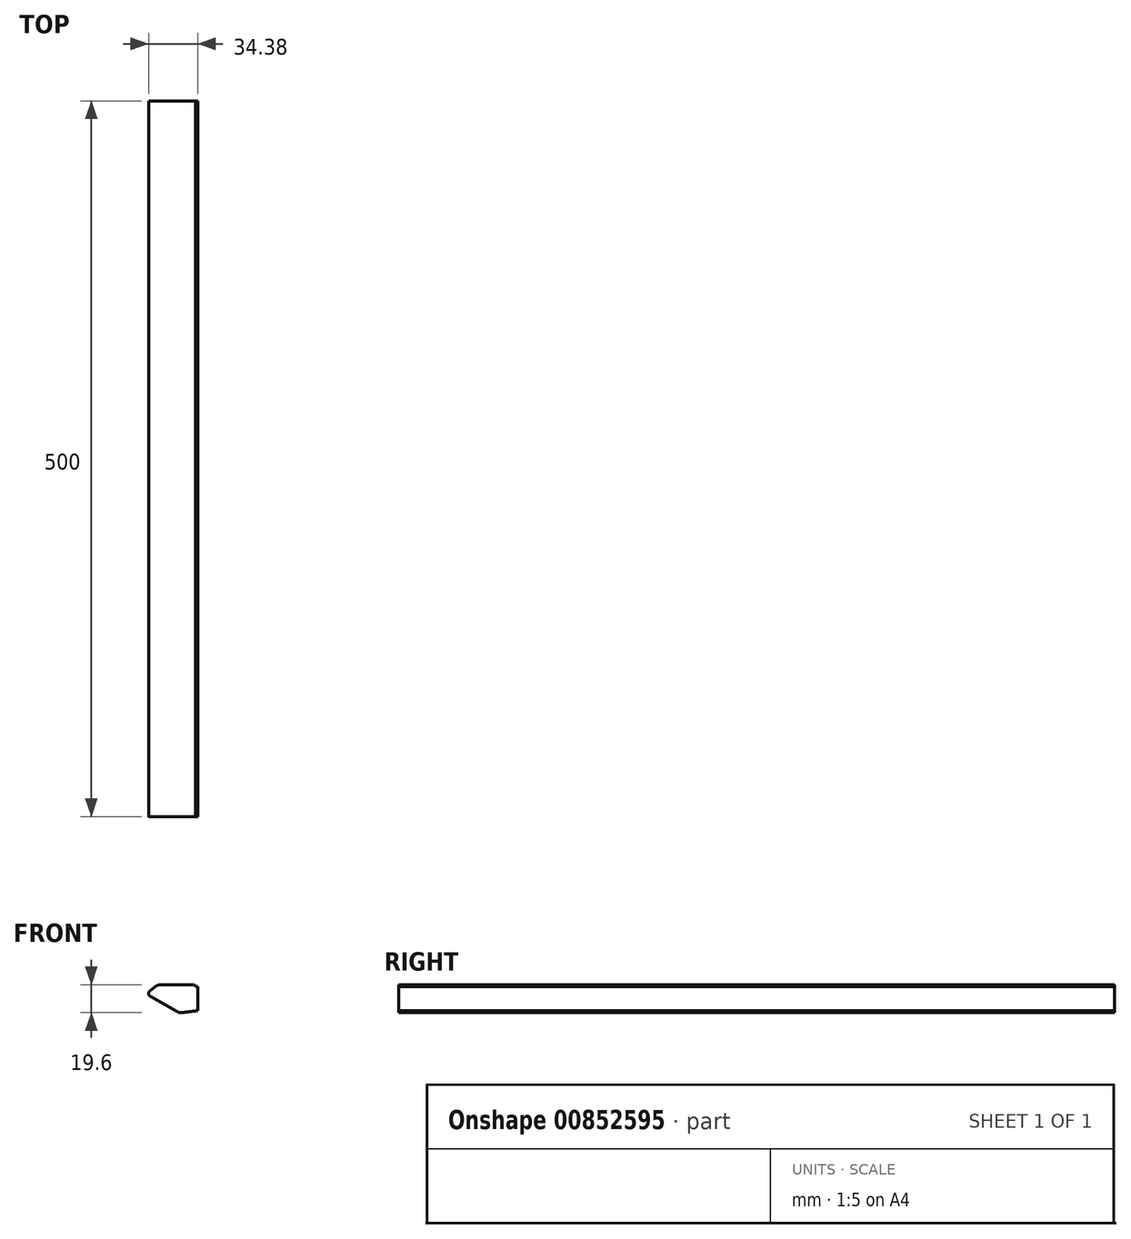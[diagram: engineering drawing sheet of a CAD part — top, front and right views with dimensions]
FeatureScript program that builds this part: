
annotation { "Feature Type Name" : "Feature", "Feature Type Description" : "" }
export const myFeature = defineFeature(function(context is Context, id is Id, definition is map)
    precondition{}
    {
        {
            var Q0;
            Q0=qCreatedBy(makeId("Front.planeOp"),FACE);
            var sketch = newSketch(context, id + "F0", { "sketchPlane" : qUnion([Q0])});
            skLineSegment(sketch, "E0", {"start": v(0, 0) * mm, "end": v(0, 72.87) * mm, "construction": true});
            skLineSegment(sketch, "E1", {"start": v(0, 0) * mm, "end": v(0, -52.15) * mm, "construction": true});
            skLineSegment(sketch, "E2", {"start": v(0, 0) * mm, "end": v(22.5, 0) * mm});
            skLineSegment(sketch, "E3", {"start": v(22.5, 0) * mm, "end": v(22.5, 1.3) * mm});
            skLineSegment(sketch, "E4", {"start": v(22.5, 1.3) * mm, "end": v(49.84, 1.3) * mm});
            skLineSegment(sketch, "E5", {"start": v(49.84, 1.3) * mm, "end": v(57.5, -5.13) * mm});
            skLineSegment(sketch, "E6", {"start": v(57.5, -5.13) * mm, "end": v(57.5, -9.13) * mm});
            skLineSegment(sketch, "E7", {"start": v(57.5, -9.13) * mm, "end": v(34, -22.7) * mm});
            skLineSegment(sketch, "E8.MirrorCS", {"start": v(0, 0) * mm, "end": v(-22.5, 0) * mm});
            skLineSegment(sketch, "E9.MirrorCS", {"start": v(-22.5, 0) * mm, "end": v(-22.5, 1.3) * mm});
            skLineSegment(sketch, "E10.MirrorCS", {"start": v(-22.5, 1.3) * mm, "end": v(-49.84, 1.3) * mm});
            skLineSegment(sketch, "E11.MirrorCS", {"start": v(-49.84, 1.3) * mm, "end": v(-57.5, -5.13) * mm});
            skLineSegment(sketch, "E12.MirrorCS", {"start": v(-57.5, -5.13) * mm, "end": v(-57.5, -9.13) * mm});
            skLineSegment(sketch, "E13.MirrorCS", {"start": v(-57.5, -9.13) * mm, "end": v(-34, -22.7) * mm});
            skArc(sketch, "E14", {"start": v(34, -22.7) * mm, "mid": v(0, -19.8) * mm, "end": v(-34, -22.7) * mm});
            skSolve(sketch);
        }
        {
            var Q0;
            Q0=makeQuery(id+"F0.imprint","IMPRINT",FACE,{"disambiguationData":[TD([[makeQuery(id+"F0.imprint","IMPRINT",EDGE,{"derivedFrom":sQuery(id+"F0.wireOp",EDGE,"E2")}),-1.0]])]});
            extrude(context, id + "F1", {"entities" : qUnion([Q0]), "endBound" : BoundingType.SYMMETRIC, "depth" : 500 * mm, "offsetDistance" : 25 * mm});
        }
        {
            var Q0;
            Q0=qCreatedBy(makeId("Front.planeOp"),FACE);
            var sketch = newSketch(context, id + "F2", { "sketchPlane" : qUnion([Q0])});
            skLineSegment(sketch, "E15.bottom", {"start": v(-19, -2) * mm, "end": v(19, -2) * mm});
            skLineSegment(sketch, "E15.top", {"start": v(-19, -15) * mm, "end": v(19, -15) * mm});
            skLineSegment(sketch, "E15.left", {"start": v(-19, -2) * mm, "end": v(-19, -15) * mm});
            skLineSegment(sketch, "E15.right", {"start": v(19, -2) * mm, "end": v(19, -15) * mm});
            skSolve(sketch);
        }
        {
            var Q0;
            Q0 = qSketchRegion(id + "F2", true);
            extrude(context, id + "F3", {"entities" : qUnion([Q0]), "operationType" : NewBodyOperationType.REMOVE, "endBound" : BoundingType.SYMMETRIC, "oppositeDirection" : true, "depth" : 500 * mm, "offsetDistance" : 25 * mm});
        }
        {
            var Q0;
            Q0=makeQuery(id+"F1.opExtrude","SWEPT_EDGE",EDGE,{"disambiguationData":[OSD([sQuery(id+"F0.wireOp",EDGE,"E9.MirrorCS"),sQuery(id+"F0.wireOp",EDGE,"E10.MirrorCS")])]});
            var Q1;
            Q1=makeQuery(id+"F1.opExtrude","SWEPT_EDGE",EDGE,{"disambiguationData":[OSD([sQuery(id+"F0.wireOp",EDGE,"E3"),sQuery(id+"F0.wireOp",EDGE,"E4")])]});
            fillet(context, id + "F4", {"entities" : qUnion([Q0, Q1]), "radius" : 2 * mm, "tangentPropagation" : true, "allowEdgeOverflow" : false});
        }
        {
            var Q0;
            Q0=makeQuery(id+"F1.opExtrude","SWEPT_EDGE",EDGE,{"disambiguationData":[OSD([sQuery(id+"F0.wireOp",EDGE,"E10.MirrorCS"),sQuery(id+"F0.wireOp",EDGE,"E11.MirrorCS")])]});
            var Q1;
            Q1=makeQuery(id+"F1.opExtrude","SWEPT_EDGE",EDGE,{"disambiguationData":[OSD([sQuery(id+"F0.wireOp",EDGE,"E4"),sQuery(id+"F0.wireOp",EDGE,"E5")])]});
            var Q2;
            Q2=makeQuery(id+"F1.opExtrude","SWEPT_EDGE",EDGE,{"disambiguationData":[OSD([sQuery(id+"F0.wireOp",EDGE,"E7"),sQuery(id+"F0.wireOp",EDGE,"E14")])]});
            var Q3;
            Q3=makeQuery(id+"F1.opExtrude","SWEPT_EDGE",EDGE,{"disambiguationData":[OSD([sQuery(id+"F0.wireOp",EDGE,"E13.MirrorCS"),sQuery(id+"F0.wireOp",EDGE,"E14")])]});
            fillet(context, id + "F5", {"entities" : qUnion([Q0, Q1, Q2, Q3]), "radius" : 9 * mm, "tangentPropagation" : true, "allowEdgeOverflow" : false});
        }
        {
            var Q0;
            Q0=makeQuery(id+"F1.opExtrude","SWEPT_EDGE",EDGE,{"disambiguationData":[OSD([sQuery(id+"F0.wireOp",EDGE,"E11.MirrorCS"),sQuery(id+"F0.wireOp",EDGE,"E12.MirrorCS")])]});
            var Q1;
            Q1=makeQuery(id+"F1.opExtrude","SWEPT_EDGE",EDGE,{"disambiguationData":[OSD([sQuery(id+"F0.wireOp",EDGE,"E5"),sQuery(id+"F0.wireOp",EDGE,"E6")])]});
            var Q2;
            Q2=makeQuery(id+"F1.opExtrude","SWEPT_EDGE",EDGE,{"disambiguationData":[OSD([sQuery(id+"F0.wireOp",EDGE,"E6"),sQuery(id+"F0.wireOp",EDGE,"E7")])]});
            var Q3;
            Q3=makeQuery(id+"F1.opExtrude","SWEPT_EDGE",EDGE,{"disambiguationData":[OSD([sQuery(id+"F0.wireOp",EDGE,"E12.MirrorCS"),sQuery(id+"F0.wireOp",EDGE,"E13.MirrorCS")])]});
            fillet(context, id + "F6", {"entities" : qUnion([Q0, Q1, Q2, Q3]), "radius" : 1 * mm, "tangentPropagation" : true, "allowEdgeOverflow" : false});
        }
        {
            var Q0;
            Q0=qCreatedBy(makeId("Front.planeOp"),FACE);
            var sketch = newSketch(context, id + "F7", { "sketchPlane" : qUnion([Q0])});
            skLineSegment(sketch, "E16.0.0", {"start": v(36.78, -21.1) * mm, "end": v(57, -9.42) * mm});
            skArc(sketch, "E16.0.1", {"start": v(57, -9.42) * mm, "mid": v(57.37, -9.05) * mm, "end": v(57.5, -8.55) * mm});
            skLineSegment(sketch, "E16.0.2", {"start": v(57.5, -8.55) * mm, "end": v(57.5, -5.6) * mm});
            skArc(sketch, "E16.0.3", {"start": v(57.5, -5.6) * mm, "mid": v(57.4, -5.17) * mm, "end": v(57.14, -4.83) * mm});
            skLineSegment(sketch, "E16.0.4", {"start": v(57.14, -4.83) * mm, "end": v(52.35, -0.8) * mm});
            skArc(sketch, "E16.0.5", {"start": v(52.35, -0.8) * mm, "mid": v(49.64, 0.76) * mm, "end": v(46.56, 1.3) * mm});
            skLineSegment(sketch, "E16.0.6", {"start": v(46.56, 1.3) * mm, "end": v(24.37, 1.3) * mm});
            skArc(sketch, "E16.0.7", {"start": v(24.37, 1.3) * mm, "mid": v(23.23, 0.94) * mm, "end": v(22.5, 0) * mm});
            skLineSegment(sketch, "E16.0.8", {"start": v(22.5, 0) * mm, "end": v(-22.5, 0) * mm});
            skArc(sketch, "E16.0.9", {"start": v(-22.5, 0) * mm, "mid": v(-23.23, 0.94) * mm, "end": v(-24.37, 1.3) * mm});
            skLineSegment(sketch, "E16.0.10", {"start": v(-24.37, 1.3) * mm, "end": v(-46.56, 1.3) * mm});
            skArc(sketch, "E16.0.11", {"start": v(-46.56, 1.3) * mm, "mid": v(-49.64, 0.76) * mm, "end": v(-52.35, -0.8) * mm});
            skLineSegment(sketch, "E16.0.12", {"start": v(-52.35, -0.8) * mm, "end": v(-57.14, -4.83) * mm});
            skArc(sketch, "E16.0.13", {"start": v(-57.14, -4.83) * mm, "mid": v(-57.4, -5.17) * mm, "end": v(-57.5, -5.6) * mm});
            skLineSegment(sketch, "E16.0.14", {"start": v(-57.5, -5.6) * mm, "end": v(-57.5, -8.55) * mm});
            skArc(sketch, "E16.0.15", {"start": v(-57.5, -8.55) * mm, "mid": v(-57.37, -9.05) * mm, "end": v(-57, -9.42) * mm});
            skLineSegment(sketch, "E16.0.16", {"start": v(-57, -9.42) * mm, "end": v(-36.78, -21.1) * mm});
            skArc(sketch, "E16.0.17", {"start": v(-36.78, -21.1) * mm, "mid": v(-33.93, -22.15) * mm, "end": v(-30.89, -22.19) * mm});
            skArc(sketch, "E16.0.18", {"start": v(-30.89, -22.19) * mm, "mid": v(0, -19.8) * mm, "end": v(30.89, -22.19) * mm});
            skArc(sketch, "E16.0.19", {"start": v(30.89, -22.19) * mm, "mid": v(33.93, -22.15) * mm, "end": v(36.78, -21.1) * mm});
            skArc(sketch, "E17.0", {"start": v(-31.2, -20.21) * mm, "mid": v(-26.1, -19.48) * mm, "end": v(-21, -18.88) * mm});
            skArc(sketch, "E17.1", {"start": v(-35.78, -19.36) * mm, "mid": v(-33.56, -20.18) * mm, "end": v(-31.2, -20.21) * mm});
            skLineSegment(sketch, "E17.2", {"start": v(-24.37, -0.7) * mm, "end": v(-46.56, -0.7) * mm});
            skArc(sketch, "E17.3", {"start": v(-46.56, -0.7) * mm, "mid": v(-48.96, -1.12) * mm, "end": v(-51.06, -2.34) * mm});
            skLineSegment(sketch, "E17.4", {"start": v(-51.06, -2.34) * mm, "end": v(-54.66, -5.36) * mm});
            skLineSegment(sketch, "E17.5", {"start": v(-54.38, -8.62) * mm, "end": v(-35.78, -19.36) * mm});
            skPoint(sketch, "E18.visualSharp", {"position": v(-56.85, -7.2) * mm});
            skArc(sketch, "E18.filletArc", {"start": v(-54.66, -5.36) * mm, "mid": v(-55.37, -7.06) * mm, "end": v(-54.38, -8.62) * mm});
            skLineSegment(sketch, "E19.0", {"start": v(-21, -2) * mm, "end": v(-21, -18.88) * mm});
            skLineSegment(sketch, "E20.0", {"start": v(-21, -2) * mm, "end": v(-22.5, -2) * mm});
            skArc(sketch, "E21", {"start": v(-22.5, -2) * mm, "mid": v(-23.23, -1.06) * mm, "end": v(-24.37, -0.7) * mm});
            skLineSegment(sketch, "E22", {"start": v(0, 0) * mm, "end": v(0, -21.14) * mm, "construction": true});
            skLineSegment(sketch, "E23.MirrorCS", {"start": v(21, -2) * mm, "end": v(21, -18.88) * mm});
            skLineSegment(sketch, "E24.MirrorCS", {"start": v(21, -2) * mm, "end": v(22.5, -2) * mm});
            skArc(sketch, "E25.MirrorCS", {"start": v(22.5, -2) * mm, "mid": v(23.23, -1.06) * mm, "end": v(24.37, -0.7) * mm});
            skLineSegment(sketch, "E26.MirrorCS", {"start": v(24.37, -0.7) * mm, "end": v(46.56, -0.7) * mm});
            skArc(sketch, "E27.MirrorCS", {"start": v(46.56, -0.7) * mm, "mid": v(48.96, -1.12) * mm, "end": v(51.06, -2.34) * mm});
            skLineSegment(sketch, "E28.MirrorCS", {"start": v(51.06, -2.34) * mm, "end": v(54.66, -5.36) * mm});
            skArc(sketch, "E29.MirrorCS", {"start": v(54.66, -5.36) * mm, "mid": v(55.37, -7.06) * mm, "end": v(54.38, -8.62) * mm});
            skLineSegment(sketch, "E30.MirrorCS", {"start": v(54.38, -8.62) * mm, "end": v(35.78, -19.36) * mm});
            skArc(sketch, "E31.MirrorCS", {"start": v(35.78, -19.36) * mm, "mid": v(33.56, -20.18) * mm, "end": v(31.2, -20.21) * mm});
            skArc(sketch, "E32.MirrorCS", {"start": v(31.2, -20.21) * mm, "mid": v(26.1, -19.48) * mm, "end": v(21, -18.88) * mm});
            skSolve(sketch);
        }
        {
            var Q0;
            Q0=makeQuery(id+"F7.imprint","IMPRINT",FACE,{"disambiguationData":[TD([[makeQuery(id+"F7.imprint","IMPRINT",EDGE,{"derivedFrom":sQuery(id+"F7.wireOp",EDGE,"E17.0")}),1.0]])]});
            var Q1;
            Q1=makeQuery(id+"F7.imprint","IMPRINT",FACE,{"disambiguationData":[TD([[makeQuery(id+"F7.imprint","IMPRINT",EDGE,{"derivedFrom":sQuery(id+"F7.wireOp",EDGE,"E23.MirrorCS")}),1.0]])]});
            extrude(context, id + "F8", {"entities" : qUnion([Q0, Q1]), "operationType" : NewBodyOperationType.REMOVE, "endBound" : BoundingType.SYMMETRIC, "oppositeDirection" : true, "depth" : 500 * mm, "offsetDistance" : 25 * mm});
        }
    });
